# Revit family: Sink-Undermount_Kitchen-KALLISTA-Voussoir-L39742-1
name_source: partatom
category: Plumbing Fixtures
units: mm (PartAtom-declared; Revit-internal decimal feet)

## family parameters
Cut with Voids When Loaded = No
Host = Face
Maintain Annotation Orientation = No
OmniClass Number = 23.31.13.00
OmniClass Title = Sinks
Part Type = Normal
Room Calculation Point = No
Round Connector Dimension = Use Diameter
Shared = No

## types (6) — shared parameters
ADA Compliant = No
Assembly Code = D2010400
CW Connection = No
Cold Water Inlet = Cold Water Inlet
Date Modified = 09/23/2025
Default Elevation = 36"
Description = 36 Inch Butler Entertainment Sink
Drain Included = No
HW Connection = No
Height = 9 3/4"
Hot Water Inlet = Hot Water Inlet
Length = 35 1/2"
Manufacturer = Kallista Co.
Master Format 2014 = 22 41 16
Master Format 2014 Name = Residential Lavatories and Sinks
Material = Natural Stone
Product Name = Voussoir
URL = https://www.kallista.com
Vent Connection = No
Waste Connection = Yes
Waste Water Outlet = Waste Water Outlet
WaterSense Certified = No
Width = 19 1/2"

## per-type parameters (varying)
| type | Finish | Model | Type |
| NM-Nero Marquina | Kohler-Stone-NM-Nero_Marquina | L39742-00-NM | 4 |
| CCV-Calacatta Viola | KALLISTA-Stone-CCV-Calacatta_Viola | L39742-00-CCV | 1 |
| FWG-Fusion Green Quartzite | KALLISTA-Stone-FWG-Fusion_Green_Quartzite | L39742-00-FWG | 2 |
| MVV-Macchia Vecchia | KALLISTA-Stone-MVV-Macchia_Vecchia | L39742-00-MVV | 3 |
| RM-Crema Marfil | KALLISTA-Stone-RM-Crema_Marfil | L39742-00-RM | 5 |
| WH-White Carrara Marble | KALLISTA-Stone-WH-White_Carrara_Marble | L39742-00-WH | 6 |

## geometry (parser evidence)
native form markers: Sweep x5
no freeform markers — native parametric forms only
